# Revit family: ASH_Contour21_S0831_BIM_GB
name_source: partatom
category: Plumbing Fixtures
units: mm (PartAtom-declared; Revit-internal decimal feet)

## family parameters
Cut with Voids When Loaded = No
Host = Face
OmniClass Number = 23.45.05.14.21.11
OmniClass Title = Bath/Shower Units
Part Type = Normal
Room Calculation Point = No
Round Connector Dimension = Use Diameter
Shared = Yes

## types (2) — shared parameters
Accessories = www.idealspec.co.uk
AreaUnits = millimeters
Assembly Code = C1030200
AssetType = Fixed
BREEAM = No
Brand = Armitage Shanks
Category = Grab Rails
Classification = Grab Rails
ConnectionType = Mechanical
CurrentRevision = 1
Default Elevation = 850 mm  [stored 2.78871 ft]
Description = Contour 21 Contemporary grab rail 45cm long
DurationUnit = year
ECA = No
ExpectedLife = 30
Features = Contemporary grab rail 45cm long
IfcExportAs = IfcFurnitureType
IfcExportType = GRABRAILS
InstallationInstructions = www.idealspec.co.uk/resources.html
LinearUnits = millimeters
MaintenanceInformation = Contemporary 21 Grab Rails | Rails and Hinged Supports | Adjustable Brackets and Grab Rails | Bluebook (idealspec.co.uk)
Manufacturer = Ideal Standard (UK) Ltd
ManufacturerURL = www.idealspec.co.uk
ModelReference = Contour 21 Contemporary grab rail 45cm long
NBSDescription = Aluminium handrails
NBSReference = 45-70-70/465
Name = ISI_GrabBars_Contour21_S0831_IdealStandard
NettWeight = 4,21 KG
NominalDepth = 98 mm
NominalHeight = 85 mm
NominalLength = 455 mm  [stored 1.49278 ft]
Product certification = https://www.idealspec.co.uk
ProductInformation = www.idealspec.co.uk/assets/datasheet/S0831
Shape = cylindrical
Size = 455 x 98 x 85 mm
Space = Internal
SpareParts = www.fastpart-spares.co.uk
TMV3 = No
URL = www.idealspec.co.uk
Uniclass2015Code = Pr_25_30_36_34
Uniclass2015Description = Grab rails
Uniclass2015Reference = Pr_25_30_36_34
Uniclass2015Title = Grab rails
Uniclass2015Version = v1.25
Version = 1
VolumeUnits = Litres
WRAS = No
WarrantyDescription = Manufacturers Warranty
WarrantyDurationParts = 5
WarrantyDurationUnit = year
WaterEfficientProduct = No
zero-valued in all types: NominalWidth

## per-type parameters (varying)
| type | BIMObjectName | BarCode | Color | Finish | MainColor | Material | Model | ModelNumber |
| S0831AA - GRABRAIL 600 CHROME STRGHT 45 | ISI_IdealStandard_GrabBars_S0831 | 5017830546115 | Chorme | Chorme | Chorme | ISI_IdealStandard_Sanitaryware_Chrome_Render | S0831AA | S0831AA |
| S0831MY - GRABRAIL 600 STAINLESS STEEL STRGHT 45 | ISI_IdealStandard_GrabBars_S0832 | 5017830546122 | Stainless Steel | Stainless Steel | Stainless Steel | ISI_IdealStandard_Sanitaryware_StainlessSteel_Render | S0831MY | S0831MY |

note: [stored X ft] marks values corroborated as IEEE doubles in the binary element streams (Revit-internal decimal feet)

## geometry (parser evidence)
native form markers: Sweep x1
no freeform markers — native parametric forms only
